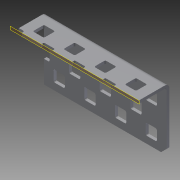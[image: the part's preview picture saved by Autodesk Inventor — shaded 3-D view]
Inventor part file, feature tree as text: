
AUTODESK INVENTOR PART (.ipt)
format: ipt  version: 2012 (Build 160160000, 160)  size: 776,192 bytes
history: native  units: in
note: dims shown in document units (in); Inventor stores cm internally (conversion verified against a paired STEP export)
features: plane x2, split x2, other x1, imported_body x1
ambient origin geometry x8: Origin, YZ Plane, XZ Plane, XY Plane, X Axis, Y Axis, Z Axis, Center Point
feature tree (6):
  parser-record x1  (decoder bookkeeping rows leaked as tree rows — omitted from the tree; the rows remain in map.json)
  imported_body  "Base1"
  plane  "Work Plane1"
  split  "Split1"
  plane  "Work Plane2"
  split  "Split2"
